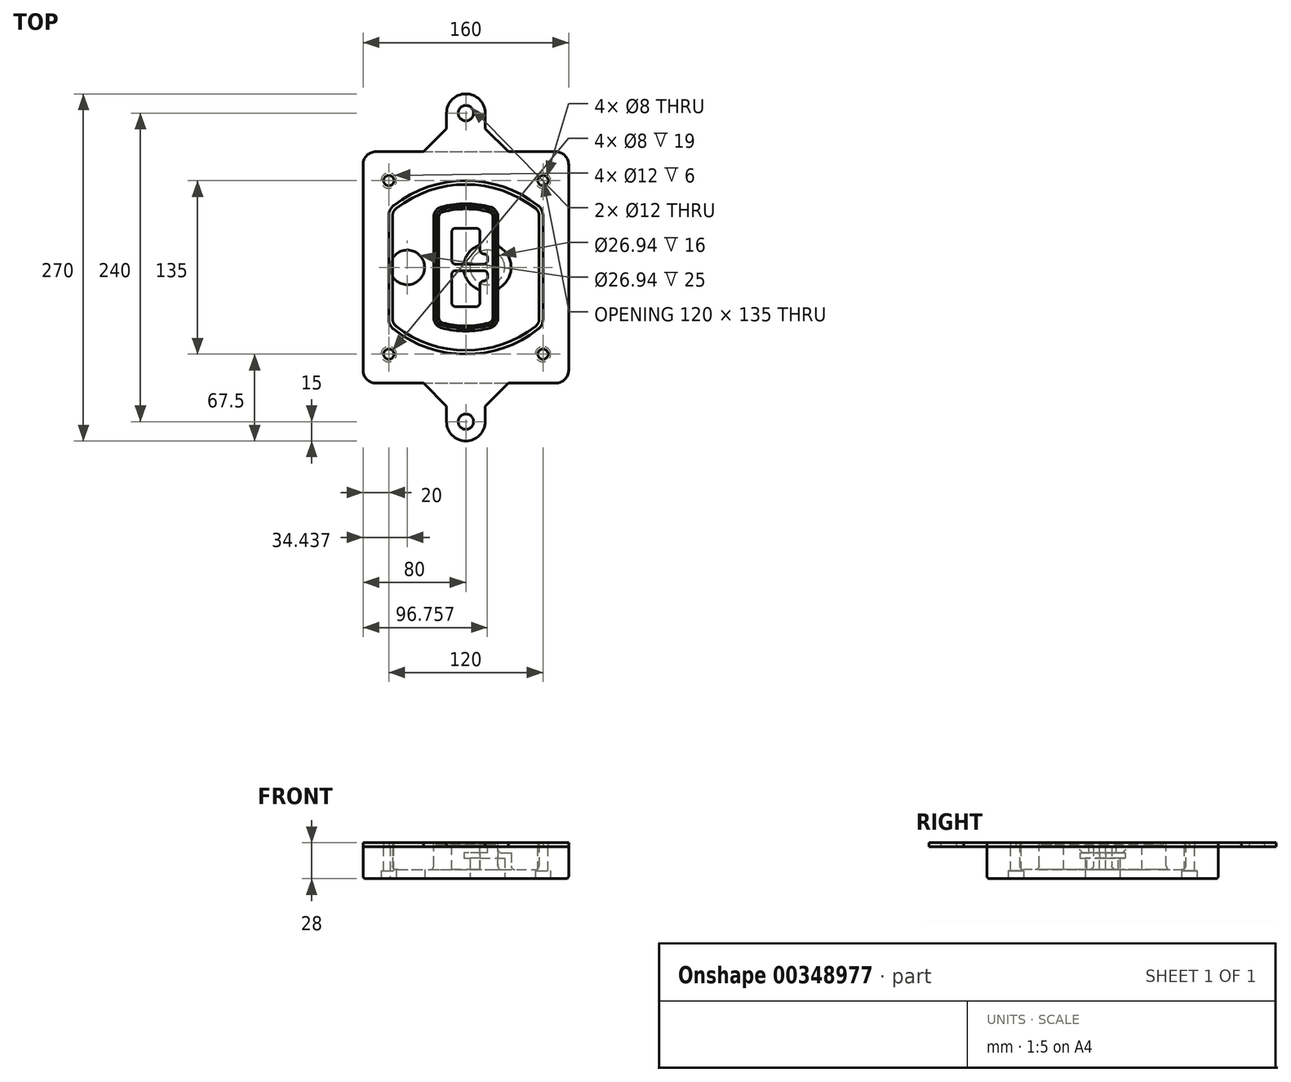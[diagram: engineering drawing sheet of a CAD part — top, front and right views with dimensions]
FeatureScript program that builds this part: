
annotation { "Feature Type Name" : "Feature", "Feature Type Description" : "" }
export const myFeature = defineFeature(function(context is Context, id is Id, definition is map)
    precondition{}
    {
        {
            var Q0;
            Q0=qCreatedBy(makeId("Top.planeOp"),FACE);
            var sketch = newSketch(context, id + "F0", { "sketchPlane" : qUnion([Q0])});
            skPoint(sketch, "E0.rect.middle", {"position": v(0, 0) * mm});
            skLineSegment(sketch, "E1.bottom", {"start": v(-70, -90) * mm, "end": v(70, -90) * mm});
            skLineSegment(sketch, "E1.top", {"start": v(-70, 90) * mm, "end": v(70, 90) * mm});
            skLineSegment(sketch, "E1.left", {"start": v(-80, -80) * mm, "end": v(-80, 80) * mm});
            skLineSegment(sketch, "E1.right", {"start": v(80, -80) * mm, "end": v(80, 80) * mm});
            skLineSegment(sketch, "E2", {"start": v(-80, 90) * mm, "end": v(80, -90) * mm, "construction": true});
            skLineSegment(sketch, "E3", {"start": v(80, 90) * mm, "end": v(-80, -90) * mm, "construction": true});
            skCircle(sketch, "E4", {"center": v(-60, 67.5) * mm, "radius": 4 * mm});
            skCircle(sketch, "E5", {"center": v(60, 67.5) * mm, "radius": 4 * mm});
            skCircle(sketch, "E6", {"center": v(60, -67.5) * mm, "radius": 4 * mm});
            skCircle(sketch, "E7", {"center": v(-60, -67.5) * mm, "radius": 4 * mm});
            skLineSegment(sketch, "E8", {"start": v(-60, 67.5) * mm, "end": v(60, 67.5) * mm, "construction": true});
            skLineSegment(sketch, "E9", {"start": v(60, 67.5) * mm, "end": v(60, -67.5) * mm, "construction": true});
            skLineSegment(sketch, "E10", {"start": v(60, -67.5) * mm, "end": v(-60, -67.5) * mm, "construction": true});
            skLineSegment(sketch, "E11", {"start": v(-60, -67.5) * mm, "end": v(-60, 67.5) * mm, "construction": true});
            skLineSegment(sketch, "E12", {"start": v(-60, 40.3) * mm, "end": v(-60, -40.3) * mm});
            skLineSegment(sketch, "E13", {"start": v(60, 40.3) * mm, "end": v(60, -40.3) * mm});
            skArc(sketch, "E14", {"start": v(56.15, 48.18) * mm, "mid": v(0, 67.5) * mm, "end": v(-56.15, 48.18) * mm});
            skArc(sketch, "E15", {"start": v(-56.15, -48.18) * mm, "mid": v(0, -67.5) * mm, "end": v(56.15, -48.18) * mm});
            skLineSegment(sketch, "E16", {"start": v(-60, 0) * mm, "end": v(60, 0) * mm, "construction": true});
            skPoint(sketch, "E17.visualSharp", {"position": v(-60, -45) * mm});
            skArc(sketch, "E17.filletArc", {"start": v(-60, -40.3) * mm, "mid": v(-58.99, -44.68) * mm, "end": v(-56.15, -48.18) * mm});
            skPoint(sketch, "E18.visualSharp", {"position": v(-60, 45) * mm});
            skArc(sketch, "E18.filletArc", {"start": v(-56.15, 48.18) * mm, "mid": v(-58.99, 44.68) * mm, "end": v(-60, 40.3) * mm});
            skPoint(sketch, "E19.visualSharp", {"position": v(60, 45) * mm});
            skArc(sketch, "E19.filletArc", {"start": v(60, 40.3) * mm, "mid": v(58.99, 44.68) * mm, "end": v(56.15, 48.18) * mm});
            skPoint(sketch, "E20.visualSharp", {"position": v(60, -45) * mm});
            skArc(sketch, "E20.filletArc", {"start": v(56.15, -48.18) * mm, "mid": v(58.99, -44.68) * mm, "end": v(60, -40.3) * mm});
            skPoint(sketch, "E21.visualSharp", {"position": v(-80, 90) * mm});
            skArc(sketch, "E21.filletArc", {"start": v(-70, 90) * mm, "mid": v(-77.07, 87.07) * mm, "end": v(-80, 80) * mm});
            skPoint(sketch, "E22.visualSharp", {"position": v(80, 90) * mm});
            skArc(sketch, "E22.filletArc", {"start": v(80, 80) * mm, "mid": v(77.07, 87.07) * mm, "end": v(70, 90) * mm});
            skPoint(sketch, "E23.visualSharp", {"position": v(80, -90) * mm});
            skArc(sketch, "E23.filletArc", {"start": v(70, -90) * mm, "mid": v(77.07, -87.07) * mm, "end": v(80, -80) * mm});
            skPoint(sketch, "E24.visualSharp", {"position": v(-80, -90) * mm});
            skArc(sketch, "E24.filletArc", {"start": v(-80, -80) * mm, "mid": v(-77.07, -87.07) * mm, "end": v(-70, -90) * mm});
            skArc(sketch, "E25.0", {"start": v(57, 40.3) * mm, "mid": v(56.3, 43.36) * mm, "end": v(54.3, 45.81) * mm});
            skLineSegment(sketch, "E25.1", {"start": v(57, 40.3) * mm, "end": v(57, -40.3) * mm});
            skArc(sketch, "E25.2", {"start": v(54.3, -45.81) * mm, "mid": v(56.3, -43.36) * mm, "end": v(57, -40.3) * mm});
            skArc(sketch, "E25.3", {"start": v(-54.3, -45.81) * mm, "mid": v(0, -64.5) * mm, "end": v(54.3, -45.81) * mm});
            skArc(sketch, "E25.4", {"start": v(-57, -40.3) * mm, "mid": v(-56.3, -43.36) * mm, "end": v(-54.3, -45.81) * mm});
            skArc(sketch, "E25.5", {"start": v(54.3, 45.81) * mm, "mid": v(0, 64.5) * mm, "end": v(-54.3, 45.81) * mm});
            skLineSegment(sketch, "E25.6", {"start": v(-57, 40.3) * mm, "end": v(-57, -40.3) * mm});
            skArc(sketch, "E25.7", {"start": v(-54.3, 45.81) * mm, "mid": v(-56.3, 43.36) * mm, "end": v(-57, 40.3) * mm});
            skArc(sketch, "E26.0", {"start": v(-58.62, 51.33) * mm, "mid": v(-62.58, 46.43) * mm, "end": v(-64, 40.3) * mm});
            skArc(sketch, "E26.1", {"start": v(58.62, 51.33) * mm, "mid": v(0, 71.5) * mm, "end": v(-58.62, 51.33) * mm});
            skArc(sketch, "E26.2", {"start": v(64, 40.3) * mm, "mid": v(62.58, 46.43) * mm, "end": v(58.62, 51.33) * mm});
            skLineSegment(sketch, "E26.3", {"start": v(64, 40.3) * mm, "end": v(64, -40.3) * mm});
            skArc(sketch, "E26.4", {"start": v(58.62, -51.33) * mm, "mid": v(62.58, -46.43) * mm, "end": v(64, -40.3) * mm});
            skLineSegment(sketch, "E26.5", {"start": v(-64, 40.3) * mm, "end": v(-64, -40.3) * mm});
            skArc(sketch, "E26.6", {"start": v(-58.62, -51.33) * mm, "mid": v(0, -71.5) * mm, "end": v(58.62, -51.33) * mm});
            skArc(sketch, "E26.7", {"start": v(-64, -40.3) * mm, "mid": v(-62.58, -46.43) * mm, "end": v(-58.62, -51.33) * mm});
            skSolve(sketch);
        }
        {
            var Q0;
            Q0=makeQuery(id+"F0.imprint","IMPRINT",FACE,{"disambiguationData":[TD([[makeQuery(id+"F0.imprint","IMPRINT",EDGE,{"derivedFrom":sQuery(id+"F0.wireOp",EDGE,"E1.bottom")}),1.0]])]});
            var Q1;
            Q1=makeQuery(id+"F0.imprint","IMPRINT",FACE,{"disambiguationData":[TD([[makeQuery(id+"F0.imprint","IMPRINT",EDGE,{"derivedFrom":sQuery(id+"F0.wireOp",EDGE,"E12")}),1.0]])]});
            var Q2;
            Q2=makeQuery(id+"F0.imprint","IMPRINT",FACE,{"disambiguationData":[TD([[makeQuery(id+"F0.imprint","IMPRINT",EDGE,{"derivedFrom":sQuery(id+"F0.wireOp",EDGE,"E25.0")}),1.0]])]});
            var Q3;
            Q3=makeQuery(id+"F0.imprint","IMPRINT",FACE,{"disambiguationData":[TD([[makeQuery(id+"F0.imprint","IMPRINT",EDGE,{"derivedFrom":sQuery(id+"F0.wireOp",EDGE,"E12")}),-1.0]])]});
            extrude(context, id + "F1", {"entities" : qUnion([Q0, Q1, Q2, Q3]), "oppositeDirection" : true, "depth" : 25 * mm});
        }
        {
            var Q0;
            Q0=makeQuery(id+"F0.imprint","IMPRINT",FACE,{"disambiguationData":[TD([[makeQuery(id+"F0.imprint","IMPRINT",EDGE,{"derivedFrom":sQuery(id+"F0.wireOp",EDGE,"E12")}),1.0]])]});
            extrude(context, id + "F2", {"entities" : qUnion([Q0]), "operationType" : NewBodyOperationType.ADD, "depth" : 3 * mm});
        }
        {
            var Q0;
            Q0=makeQuery(id+"F0.imprint","IMPRINT",FACE,{"disambiguationData":[TD([[makeQuery(id+"F0.imprint","IMPRINT",EDGE,{"derivedFrom":sQuery(id+"F0.wireOp",EDGE,"E25.0")}),1.0]])]});
            extrude(context, id + "F3", {"entities" : qUnion([Q0]), "operationType" : NewBodyOperationType.REMOVE, "oppositeDirection" : true, "depth" : 18 * mm});
        }
        {
            var Q0;
            Q0=makeQuery(id+"F2.opExtrude","CAP_FACE",FACE,{"disambiguationData":[OSD([sQuery(id+"F0.wireOp",EDGE,"E12"),sQuery(id+"F0.wireOp",EDGE,"E13"),sQuery(id+"F0.wireOp",EDGE,"E14"),sQuery(id+"F0.wireOp",EDGE,"E15"),sQuery(id+"F0.wireOp",EDGE,"E17.filletArc"),sQuery(id+"F0.wireOp",EDGE,"E18.filletArc"),sQuery(id+"F0.wireOp",EDGE,"E19.filletArc"),sQuery(id+"F0.wireOp",EDGE,"E20.filletArc"),sQuery(id+"F0.wireOp",EDGE,"E25.0"),sQuery(id+"F0.wireOp",EDGE,"E25.1"),sQuery(id+"F0.wireOp",EDGE,"E25.2"),sQuery(id+"F0.wireOp",EDGE,"E25.3"),sQuery(id+"F0.wireOp",EDGE,"E25.4"),sQuery(id+"F0.wireOp",EDGE,"E25.5"),sQuery(id+"F0.wireOp",EDGE,"E25.6"),sQuery(id+"F0.wireOp",EDGE,"E25.7")])],"isStart":false});
            var sketch = newSketch(context, id + "F4", { "sketchPlane" : qUnion([Q0])});
            skArc(sketch, "E27.0", {"start": v(-19.08, -46.97) * mm, "mid": v(0, -49.5) * mm, "end": v(19.08, -46.97) * mm});
            skArc(sketch, "E28.0", {"start": v(19.08, 46.97) * mm, "mid": v(0, 49.5) * mm, "end": v(-19.08, 46.97) * mm});
            skLineSegment(sketch, "E29", {"start": v(-25, 39.25) * mm, "end": v(-25, -39.25) * mm});
            skLineSegment(sketch, "E30", {"start": v(25, 39.25) * mm, "end": v(25, -39.25) * mm});
            skLineSegment(sketch, "E31", {"start": v(-25, 45.1) * mm, "end": v(25, 45.1) * mm, "construction": true});
            skLineSegment(sketch, "E32", {"start": v(-25, -45.1) * mm, "end": v(25, -45.1) * mm, "construction": true});
            skPoint(sketch, "E33.visualSharp", {"position": v(-25, 45.1) * mm});
            skArc(sketch, "E33.filletArc", {"start": v(-19.08, 46.97) * mm, "mid": v(-23.35, 44.11) * mm, "end": v(-25, 39.25) * mm});
            skPoint(sketch, "E34.visualSharp", {"position": v(25, 45.1) * mm});
            skArc(sketch, "E34.filletArc", {"start": v(25, 39.25) * mm, "mid": v(23.35, 44.11) * mm, "end": v(19.08, 46.97) * mm});
            skPoint(sketch, "E35.visualSharp", {"position": v(25, -45.1) * mm});
            skArc(sketch, "E35.filletArc", {"start": v(19.08, -46.97) * mm, "mid": v(23.35, -44.11) * mm, "end": v(25, -39.25) * mm});
            skPoint(sketch, "E36.visualSharp", {"position": v(-25, -45.1) * mm});
            skArc(sketch, "E36.filletArc", {"start": v(-25, -39.25) * mm, "mid": v(-23.35, -44.11) * mm, "end": v(-19.08, -46.97) * mm});
            skArc(sketch, "E37.0", {"start": v(54.3, 45.81) * mm, "mid": v(0, 64.5) * mm, "end": v(-54.3, 45.81) * mm});
            skArc(sketch, "E37.1", {"start": v(-54.3, 45.81) * mm, "mid": v(-56.3, 43.36) * mm, "end": v(-57, 40.3) * mm});
            skLineSegment(sketch, "E37.2", {"start": v(-57, 40.3) * mm, "end": v(-57, -40.3) * mm});
            skArc(sketch, "E37.3", {"start": v(-57, -40.3) * mm, "mid": v(-56.3, -43.36) * mm, "end": v(-54.3, -45.81) * mm});
            skArc(sketch, "E37.4", {"start": v(-54.3, -45.81) * mm, "mid": v(0, -64.5) * mm, "end": v(54.3, -45.81) * mm});
            skArc(sketch, "E37.5", {"start": v(54.3, -45.81) * mm, "mid": v(56.3, -43.36) * mm, "end": v(57, -40.3) * mm});
            skLineSegment(sketch, "E37.6", {"start": v(57, 40.3) * mm, "end": v(57, -40.3) * mm});
            skArc(sketch, "E37.7", {"start": v(57, 40.3) * mm, "mid": v(56.3, 43.36) * mm, "end": v(54.3, 45.81) * mm});
            skLineSegment(sketch, "E38.0", {"start": v(23, 39.25) * mm, "end": v(23, -39.25) * mm});
            skArc(sketch, "E38.1", {"start": v(18.56, -45.04) * mm, "mid": v(21.76, -42.9) * mm, "end": v(23, -39.25) * mm});
            skArc(sketch, "E38.2", {"start": v(-18.56, -45.04) * mm, "mid": v(0, -47.5) * mm, "end": v(18.56, -45.04) * mm});
            skArc(sketch, "E38.3", {"start": v(-23, -39.25) * mm, "mid": v(-21.76, -42.9) * mm, "end": v(-18.56, -45.04) * mm});
            skLineSegment(sketch, "E38.4", {"start": v(-23, 39.25) * mm, "end": v(-23, -39.25) * mm});
            skArc(sketch, "E38.5", {"start": v(23, 39.25) * mm, "mid": v(21.76, 42.9) * mm, "end": v(18.56, 45.04) * mm});
            skArc(sketch, "E38.6", {"start": v(-18.56, 45.04) * mm, "mid": v(-21.76, 42.9) * mm, "end": v(-23, 39.25) * mm});
            skArc(sketch, "E38.7", {"start": v(18.56, 45.04) * mm, "mid": v(0, 47.5) * mm, "end": v(-18.56, 45.04) * mm});
            skArc(sketch, "E39.0", {"start": v(21, 39.25) * mm, "mid": v(20.18, 41.68) * mm, "end": v(18.04, 43.1) * mm});
            skLineSegment(sketch, "E39.1", {"start": v(21, 39.25) * mm, "end": v(21, -39.25) * mm});
            skArc(sketch, "E39.2", {"start": v(18.04, -43.1) * mm, "mid": v(20.18, -41.68) * mm, "end": v(21, -39.25) * mm});
            skArc(sketch, "E39.3", {"start": v(-18.04, -43.1) * mm, "mid": v(0, -45.5) * mm, "end": v(18.04, -43.1) * mm});
            skArc(sketch, "E39.4", {"start": v(-21, -39.25) * mm, "mid": v(-20.18, -41.68) * mm, "end": v(-18.04, -43.1) * mm});
            skArc(sketch, "E39.5", {"start": v(18.04, 43.1) * mm, "mid": v(0, 45.5) * mm, "end": v(-18.04, 43.1) * mm});
            skLineSegment(sketch, "E39.6", {"start": v(-21, 39.25) * mm, "end": v(-21, -39.25) * mm});
            skArc(sketch, "E39.7", {"start": v(-18.04, 43.1) * mm, "mid": v(-20.18, 41.68) * mm, "end": v(-21, 39.25) * mm});
            skLineSegment(sketch, "E40", {"start": v(-25, 0) * mm, "end": v(25, 0) * mm, "construction": true});
            skLineSegment(sketch, "E41", {"start": v(-11, 5.5) * mm, "end": v(-11, 27.5) * mm});
            skLineSegment(sketch, "E42", {"start": v(-8, 30.5) * mm, "end": v(8, 30.5) * mm});
            skLineSegment(sketch, "E43", {"start": v(11, 27.5) * mm, "end": v(11, 13.5) * mm});
            skLineSegment(sketch, "E44", {"start": v(14, 10.5) * mm, "end": v(14, 10.5) * mm});
            skLineSegment(sketch, "E45", {"start": v(17, 7.5) * mm, "end": v(17, 5.5) * mm});
            skLineSegment(sketch, "E46", {"start": v(14, 2.5) * mm, "end": v(-8, 2.5) * mm});
            skPoint(sketch, "E47.visualSharp", {"position": v(-11, 30.5) * mm});
            skArc(sketch, "E47.filletArc", {"start": v(-8, 30.5) * mm, "mid": v(-10.12, 29.62) * mm, "end": v(-11, 27.5) * mm});
            skPoint(sketch, "E48.visualSharp", {"position": v(11, 30.5) * mm});
            skArc(sketch, "E48.filletArc", {"start": v(11, 27.5) * mm, "mid": v(10.12, 29.62) * mm, "end": v(8, 30.5) * mm});
            skPoint(sketch, "E49.visualSharp", {"position": v(11, 10.5) * mm});
            skArc(sketch, "E49.filletArc", {"start": v(11, 13.5) * mm, "mid": v(11.88, 11.38) * mm, "end": v(14, 10.5) * mm});
            skPoint(sketch, "E50.visualSharp", {"position": v(17, 10.5) * mm});
            skArc(sketch, "E50.filletArc", {"start": v(17, 7.5) * mm, "mid": v(16.12, 9.62) * mm, "end": v(14, 10.5) * mm});
            skPoint(sketch, "E51.visualSharp", {"position": v(17, 2.5) * mm});
            skArc(sketch, "E51.filletArc", {"start": v(14, 2.5) * mm, "mid": v(16.12, 3.38) * mm, "end": v(17, 5.5) * mm});
            skPoint(sketch, "E52.visualSharp", {"position": v(-11, 2.5) * mm});
            skArc(sketch, "E52.filletArc", {"start": v(-11, 5.5) * mm, "mid": v(-10.12, 3.38) * mm, "end": v(-8, 2.5) * mm});
            skLineSegment(sketch, "E53.0.MirrorCS", {"start": v(14, -2.5) * mm, "end": v(-8, -2.5) * mm});
            skArc(sketch, "E54.0.MirrorCS", {"start": v(-11, -5.5) * mm, "mid": v(-10.12, -3.38) * mm, "end": v(-8, -2.5) * mm});
            skLineSegment(sketch, "E55.0.MirrorCS", {"start": v(-11, -5.5) * mm, "end": v(-11, -27.5) * mm});
            skArc(sketch, "E56.0.MirrorCS", {"start": v(-8, -30.5) * mm, "mid": v(-10.12, -29.62) * mm, "end": v(-11, -27.5) * mm});
            skLineSegment(sketch, "E57.0.MirrorCS", {"start": v(-8, -30.5) * mm, "end": v(8, -30.5) * mm});
            skArc(sketch, "E58.0.MirrorCS", {"start": v(11, -27.5) * mm, "mid": v(10.12, -29.62) * mm, "end": v(8, -30.5) * mm});
            skLineSegment(sketch, "E59.0.MirrorCS", {"start": v(11, -27.5) * mm, "end": v(11, -13.5) * mm});
            skArc(sketch, "E60.0.MirrorCS", {"start": v(11, -13.5) * mm, "mid": v(11.88, -11.38) * mm, "end": v(14, -10.5) * mm});
            skArc(sketch, "E61.0.MirrorCS", {"start": v(17, -7.5) * mm, "mid": v(16.12, -9.62) * mm, "end": v(14, -10.5) * mm});
            skLineSegment(sketch, "E62.0.MirrorCS", {"start": v(17, -7.5) * mm, "end": v(17, -5.5) * mm});
            skArc(sketch, "E63.0.MirrorCS", {"start": v(14, -2.5) * mm, "mid": v(16.12, -3.38) * mm, "end": v(17, -5.5) * mm});
            skSolve(sketch);
        }
        {
            var Q0;
            Q0=makeQuery(id+"F4.imprint","IMPRINT",FACE,{"disambiguationData":[TD([[makeQuery(id+"F4.imprint","IMPRINT",EDGE,{"derivedFrom":sQuery(id+"F4.wireOp",EDGE,"E27.0")}),1.0]])]});
            var Q1;
            Q1=makeQuery(id+"F4.imprint","IMPRINT",FACE,{"disambiguationData":[TD([[makeQuery(id+"F4.imprint","IMPRINT",EDGE,{"derivedFrom":sQuery(id+"F4.wireOp",EDGE,"E38.0")}),-1.0]])]});
            var Q2;
            Q2=makeQuery(id+"F4.imprint","IMPRINT",FACE,{"disambiguationData":[TD([[makeQuery(id+"F4.imprint","IMPRINT",EDGE,{"derivedFrom":sQuery(id+"F4.wireOp",EDGE,"E39.0")}),1.0]])]});
            extrude(context, id + "F5", {"entities" : qUnion([Q0, Q1, Q2]), "operationType" : NewBodyOperationType.ADD, "endBound" : BoundingType.UP_TO_NEXT, "oppositeDirection" : true, "depth" : 25 * mm});
        }
        {
            var Q0;
            Q0=makeQuery(id+"F4.imprint","IMPRINT",FACE,{"disambiguationData":[TD([[makeQuery(id+"F4.imprint","IMPRINT",EDGE,{"derivedFrom":sQuery(id+"F4.wireOp",EDGE,"E38.0")}),-1.0]])]});
            extrude(context, id + "F6", {"entities" : qUnion([Q0]), "operationType" : NewBodyOperationType.REMOVE, "oppositeDirection" : true, "depth" : 2 * mm});
        }
        {
            var Q0;
            Q0=makeQuery(id+"F1.opExtrude","CAP_FACE",FACE,{"disambiguationData":[OSD([sQuery(id+"F0.wireOp",EDGE,"E1.bottom"),sQuery(id+"F0.wireOp",EDGE,"E1.top"),sQuery(id+"F0.wireOp",EDGE,"E1.left"),sQuery(id+"F0.wireOp",EDGE,"E1.right"),sQuery(id+"F0.wireOp",EDGE,"E4"),sQuery(id+"F0.wireOp",EDGE,"E5"),sQuery(id+"F0.wireOp",EDGE,"E6"),sQuery(id+"F0.wireOp",EDGE,"E7"),sQuery(id+"F0.wireOp",EDGE,"E21.filletArc"),sQuery(id+"F0.wireOp",EDGE,"E22.filletArc"),sQuery(id+"F0.wireOp",EDGE,"E23.filletArc"),sQuery(id+"F0.wireOp",EDGE,"E24.filletArc")])],"isStart":false});
            var sketch = newSketch(context, id + "F7", { "sketchPlane" : qUnion([Q0])});
            skCircle(sketch, "E64", {"center": v(16.76, 0) * mm, "radius": 13.47 * mm});
            skCircle(sketch, "E65", {"center": v(-45.56, 0) * mm, "radius": 13.47 * mm});
            skLineSegment(sketch, "E66", {"start": v(80, 0) * mm, "end": v(-80, 0) * mm});
            skCircle(sketch, "E67", {"center": v(16.76, 0) * mm, "radius": 18.47 * mm});
            skCircle(sketch, "E68", {"center": v(60, -67.5) * mm, "radius": 6 * mm});
            skCircle(sketch, "E69", {"center": v(-60, -67.5) * mm, "radius": 6 * mm});
            skCircle(sketch, "E70", {"center": v(-60, 67.5) * mm, "radius": 6 * mm});
            skCircle(sketch, "E71", {"center": v(60, 67.5) * mm, "radius": 6 * mm});
            skSolve(sketch);
        }
        {
            var Q0;
            {var subQ1=sQuery(id+"F7.wireOp",EDGE,"E66");var subQ4=sQuery(id+"F7.wireOp",EDGE,"E64");var subQ6=makeQuery(id+"F7.imprint","INTERSECT",VERTEX,{"disambiguationData":[OD(0.0)],"derivedFrom":[subQ4,subQ1]});Q0=makeQuery(id+"F7.imprint","IMPRINT",FACE,{"disambiguationData":[TD([[makeQuery(id+"F7.imprint","IMPRINT",EDGE,{"disambiguationData":[TD([[subQ6,-1.0]])],"derivedFrom":subQ4}),-1.0]])]});}
            var Q1;
            {var subQ0=sQuery(id+"F7.wireOp",EDGE,"E66");var subQ1=sQuery(id+"F7.wireOp",EDGE,"E64");var subQ3=makeQuery(id+"F7.imprint","INTERSECT",VERTEX,{"disambiguationData":[OD(0.0)],"derivedFrom":[subQ1,subQ0]});Q1=makeQuery(id+"F7.imprint","IMPRINT",FACE,{"disambiguationData":[TD([[makeQuery(id+"F7.imprint","IMPRINT",EDGE,{"disambiguationData":[TD([[subQ3,-1.0]])],"derivedFrom":subQ1}),1.0]])]});}
            var Q2;
            {var subQ0=sQuery(id+"F7.wireOp",EDGE,"E66");var subQ1=sQuery(id+"F7.wireOp",EDGE,"E64");var subQ3=makeQuery(id+"F7.imprint","INTERSECT",VERTEX,{"disambiguationData":[OD(0.0)],"derivedFrom":[subQ1,subQ0]});Q2=makeQuery(id+"F7.imprint","IMPRINT",FACE,{"disambiguationData":[TD([[makeQuery(id+"F7.imprint","IMPRINT",EDGE,{"disambiguationData":[TD([[subQ3,1.0]])],"derivedFrom":subQ1}),1.0]])]});}
            var Q3;
            {var subQ1=sQuery(id+"F7.wireOp",EDGE,"E66");var subQ4=sQuery(id+"F7.wireOp",EDGE,"E64");var subQ6=makeQuery(id+"F7.imprint","INTERSECT",VERTEX,{"disambiguationData":[OD(0.0)],"derivedFrom":[subQ4,subQ1]});Q3=makeQuery(id+"F7.imprint","IMPRINT",FACE,{"disambiguationData":[TD([[makeQuery(id+"F7.imprint","IMPRINT",EDGE,{"disambiguationData":[TD([[subQ6,1.0]])],"derivedFrom":subQ4}),-1.0]])]});}
            extrude(context, id + "F8", {"entities" : qUnion([Q0, Q1, Q2, Q3]), "operationType" : NewBodyOperationType.ADD, "oppositeDirection" : true, "depth" : 20 * mm});
        }
        {
            var Q0;
            {var subQ0=sQuery(id+"F7.wireOp",EDGE,"E66");var subQ1=sQuery(id+"F7.wireOp",EDGE,"E64");var subQ3=makeQuery(id+"F7.imprint","INTERSECT",VERTEX,{"disambiguationData":[OD(0.0)],"derivedFrom":[subQ1,subQ0]});Q0=makeQuery(id+"F7.imprint","IMPRINT",FACE,{"disambiguationData":[TD([[makeQuery(id+"F7.imprint","IMPRINT",EDGE,{"disambiguationData":[TD([[subQ3,-1.0]])],"derivedFrom":subQ1}),1.0]])]});}
            var Q1;
            {var subQ0=sQuery(id+"F7.wireOp",EDGE,"E66");var subQ1=sQuery(id+"F7.wireOp",EDGE,"E64");var subQ3=makeQuery(id+"F7.imprint","INTERSECT",VERTEX,{"disambiguationData":[OD(0.0)],"derivedFrom":[subQ1,subQ0]});Q1=makeQuery(id+"F7.imprint","IMPRINT",FACE,{"disambiguationData":[TD([[makeQuery(id+"F7.imprint","IMPRINT",EDGE,{"disambiguationData":[TD([[subQ3,1.0]])],"derivedFrom":subQ1}),1.0]])]});}
            extrude(context, id + "F9", {"entities" : qUnion([Q0, Q1]), "operationType" : NewBodyOperationType.REMOVE, "oppositeDirection" : true, "depth" : 16 * mm});
        }
        {
            var Q0;
            {var subQ0=sQuery(id+"F7.wireOp",EDGE,"E66");var subQ1=sQuery(id+"F7.wireOp",EDGE,"E65");var subQ3=makeQuery(id+"F7.imprint","INTERSECT",VERTEX,{"disambiguationData":[OD(0.0)],"derivedFrom":[subQ1,subQ0]});Q0=makeQuery(id+"F7.imprint","IMPRINT",FACE,{"disambiguationData":[TD([[makeQuery(id+"F7.imprint","IMPRINT",EDGE,{"disambiguationData":[TD([[subQ3,-1.0]])],"derivedFrom":subQ1}),1.0]])]});}
            var Q1;
            {var subQ0=sQuery(id+"F7.wireOp",EDGE,"E66");var subQ1=sQuery(id+"F7.wireOp",EDGE,"E65");var subQ3=makeQuery(id+"F7.imprint","INTERSECT",VERTEX,{"disambiguationData":[OD(0.0)],"derivedFrom":[subQ1,subQ0]});Q1=makeQuery(id+"F7.imprint","IMPRINT",FACE,{"disambiguationData":[TD([[makeQuery(id+"F7.imprint","IMPRINT",EDGE,{"disambiguationData":[TD([[subQ3,1.0]])],"derivedFrom":subQ1}),1.0]])]});}
            extrude(context, id + "F10", {"entities" : qUnion([Q0, Q1]), "operationType" : NewBodyOperationType.REMOVE, "oppositeDirection" : true, "depth" : 25 * mm});
        }
        {
            var Q0;
            Q0=makeQuery(id+"F7.imprint","IMPRINT",FACE,{"disambiguationData":[TD([[makeQuery(id+"F7.imprint","IMPRINT",EDGE,{"derivedFrom":sQuery(id+"F7.wireOp",EDGE,"E68")}),1.0]])]});
            var Q1;
            Q1=makeQuery(id+"F7.imprint","IMPRINT",FACE,{"disambiguationData":[TD([[makeQuery(id+"F7.imprint","IMPRINT",EDGE,{"derivedFrom":makeQuery(id+"F1.opExtrude","CAP_EDGE",EDGE,{"disambiguationData":[OSD([sQuery(id+"F0.wireOp",EDGE,"E5")])],"isStart":false})}),-1.0]])]});
            var Q2;
            Q2=makeQuery(id+"F7.imprint","IMPRINT",FACE,{"disambiguationData":[TD([[makeQuery(id+"F7.imprint","IMPRINT",EDGE,{"derivedFrom":sQuery(id+"F7.wireOp",EDGE,"E69")}),1.0]])]});
            var Q3;
            Q3=makeQuery(id+"F7.imprint","IMPRINT",FACE,{"disambiguationData":[TD([[makeQuery(id+"F7.imprint","IMPRINT",EDGE,{"derivedFrom":makeQuery(id+"F1.opExtrude","CAP_EDGE",EDGE,{"disambiguationData":[OSD([sQuery(id+"F0.wireOp",EDGE,"E4")])],"isStart":false})}),-1.0]])]});
            var Q4;
            Q4=makeQuery(id+"F7.imprint","IMPRINT",FACE,{"disambiguationData":[TD([[makeQuery(id+"F7.imprint","IMPRINT",EDGE,{"derivedFrom":sQuery(id+"F7.wireOp",EDGE,"E70")}),1.0]])]});
            var Q5;
            Q5=makeQuery(id+"F7.imprint","IMPRINT",FACE,{"disambiguationData":[TD([[makeQuery(id+"F7.imprint","IMPRINT",EDGE,{"derivedFrom":makeQuery(id+"F1.opExtrude","CAP_EDGE",EDGE,{"disambiguationData":[OSD([sQuery(id+"F0.wireOp",EDGE,"E7")])],"isStart":false})}),-1.0]])]});
            var Q6;
            Q6=makeQuery(id+"F7.imprint","IMPRINT",FACE,{"disambiguationData":[TD([[makeQuery(id+"F7.imprint","IMPRINT",EDGE,{"derivedFrom":sQuery(id+"F7.wireOp",EDGE,"E71")}),1.0]])]});
            var Q7;
            Q7=makeQuery(id+"F7.imprint","IMPRINT",FACE,{"disambiguationData":[TD([[makeQuery(id+"F7.imprint","IMPRINT",EDGE,{"derivedFrom":makeQuery(id+"F1.opExtrude","CAP_EDGE",EDGE,{"disambiguationData":[OSD([sQuery(id+"F0.wireOp",EDGE,"E6")])],"isStart":false})}),-1.0]])]});
            extrude(context, id + "F11", {"entities" : qUnion([Q0, Q1, Q2, Q3, Q4, Q5, Q6, Q7]), "operationType" : NewBodyOperationType.REMOVE, "oppositeDirection" : true, "depth" : 6 * mm});
        }
        {
            var Q0;
            Q0=makeQuery(id+"F9.boolean.opBoolean","COPY",FACE,{"derivedFrom":makeQuery(id+"F9.opExtrude","CAP_FACE",FACE,{"disambiguationData":[OSD([sQuery(id+"F7.wireOp",EDGE,"E64")])],"isStart":false})});
            var sketch = newSketch(context, id + "F12", { "sketchPlane" : qUnion([Q0])});
            skArc(sketch, "E72.0", {"start": v(11, 17.55) * mm, "mid": v(2.57, 11.82) * mm, "end": v(-1.54, 2.5) * mm});
            skArc(sketch, "E72.1", {"start": v(-1.54, -2.5) * mm, "mid": v(2.57, -11.82) * mm, "end": v(11, -17.55) * mm});
            skLineSegment(sketch, "E73", {"start": v(-1.54, -2.5) * mm, "end": v(14, -2.5) * mm});
            skLineSegment(sketch, "E74.0", {"start": v(14, 2.5) * mm, "end": v(-1.54, 2.5) * mm});
            skArc(sketch, "E74.1", {"start": v(14, 2.5) * mm, "mid": v(16.12, 3.38) * mm, "end": v(17, 5.5) * mm});
            skLineSegment(sketch, "E74.2", {"start": v(17, 7.5) * mm, "end": v(17, 5.5) * mm});
            skArc(sketch, "E74.3", {"start": v(17, 7.5) * mm, "mid": v(16.12, 9.62) * mm, "end": v(14, 10.5) * mm});
            skArc(sketch, "E74.4", {"start": v(11, 13.5) * mm, "mid": v(11.88, 11.38) * mm, "end": v(14, 10.5) * mm});
            skLineSegment(sketch, "E74.5", {"start": v(11, 17.55) * mm, "end": v(11, 13.5) * mm});
            skLineSegment(sketch, "E74.7", {"start": v(14, -2.5) * mm, "end": v(-1.54, -2.5) * mm});
            skArc(sketch, "E74.8", {"start": v(14, -2.5) * mm, "mid": v(16.12, -3.38) * mm, "end": v(17, -5.5) * mm});
            skLineSegment(sketch, "E74.9", {"start": v(17, -7.5) * mm, "end": v(17, -5.5) * mm});
            skArc(sketch, "E74.10", {"start": v(17, -7.5) * mm, "mid": v(16.12, -9.62) * mm, "end": v(14, -10.5) * mm});
            skArc(sketch, "E74.11", {"start": v(11, -13.5) * mm, "mid": v(11.88, -11.38) * mm, "end": v(14, -10.5) * mm});
            skLineSegment(sketch, "E74.12", {"start": v(11, -17.55) * mm, "end": v(11, -13.5) * mm});
            skPoint(sketch, "E75.orphan", {"position": v(11, -27.5) * mm});
            skPoint(sketch, "E76.orphan", {"position": v(-8, -2.5) * mm});
            skPoint(sketch, "E77.orphan", {"position": v(-8, 2.5) * mm});
            skPoint(sketch, "E78.orphan", {"position": v(11, 27.5) * mm});
            skSolve(sketch);
        }
        {
            var Q0;
            {var subQ7=sQuery(id+"F12.wireOp",EDGE,"E72.0");var subQ14=sQuery(id+"F12.wireOp",EDGE,"E72.1");var subQ16=sQuery(id+"F12.wireOp",EDGE,"E74.1");var subQ18=sQuery(id+"F12.wireOp",EDGE,"E74.8");Q0=qUnion([makeQuery(id+"F12.imprint","IMPRINT",FACE,{"disambiguationData":[TD([[makeQuery(id+"F12.imprint","IMPRINT",EDGE,{"derivedFrom":subQ7}),1.0]])]}),makeQuery(id+"F12.imprint","IMPRINT",FACE,{"disambiguationData":[TD([[makeQuery(id+"F12.imprint","IMPRINT",EDGE,{"derivedFrom":subQ14}),1.0]])]}),makeQuery(id+"F12.imprint","IMPRINT",FACE,{"disambiguationData":[TD([[makeQuery(id+"F12.imprint","IMPRINT",EDGE,{"derivedFrom":subQ16}),1.0]])]}),makeQuery(id+"F12.imprint","IMPRINT",FACE,{"disambiguationData":[TD([[makeQuery(id+"F12.imprint","IMPRINT",EDGE,{"derivedFrom":subQ18}),-1.0]])]})]);}
            var Q1;
            Q1=makeQuery(id+"F5.boolean.opBoolean","SPLIT",FACE,{"disambiguationData":[TD([makeQuery(id+"F5.opExtrude","SWEPT_FACE",FACE,{"disambiguationData":[OSD([sQuery(id+"F4.wireOp",EDGE,"E41")])]})])],"derivedFrom":makeQuery(id+"F3.boolean.opBoolean","COPY",FACE,{"derivedFrom":makeQuery(id+"F3.opExtrude","CAP_FACE",FACE,{"disambiguationData":[OSD([sQuery(id+"F0.wireOp",EDGE,"E25.0"),sQuery(id+"F0.wireOp",EDGE,"E25.1"),sQuery(id+"F0.wireOp",EDGE,"E25.2"),sQuery(id+"F0.wireOp",EDGE,"E25.3"),sQuery(id+"F0.wireOp",EDGE,"E25.4"),sQuery(id+"F0.wireOp",EDGE,"E25.5"),sQuery(id+"F0.wireOp",EDGE,"E25.6"),sQuery(id+"F0.wireOp",EDGE,"E25.7")])],"isStart":false})})});
            extrude(context, id + "F13", {"entities" : qUnion([Q0]), "operationType" : NewBodyOperationType.REMOVE, "endBound" : BoundingType.UP_TO_SURFACE, "endBoundEntityFace" : qUnion([Q1]), "depth" : 25 * mm});
        }
        {
            var Q0;
            Q0=makeQuery(id+"F3.boolean.opBoolean","COPY",EDGE,{"derivedFrom":makeQuery(id+"F3.opExtrude","CAP_EDGE",EDGE,{"disambiguationData":[OSD([sQuery(id+"F0.wireOp",EDGE,"E25.6")])],"isStart":false})});
            var Q1;
            Q1=makeQuery(id+"F8.boolean.opBoolean","INTERSECT",EDGE,{"derivedFrom":[makeQuery(id+"F5.opExtrude","SWEPT_FACE",FACE,{"disambiguationData":[OSD([sQuery(id+"F4.wireOp",EDGE,"E30")])]}),makeQuery(id+"F8.opExtrude","CAP_FACE",FACE,{"disambiguationData":[OSD([sQuery(id+"F7.wireOp",EDGE,"E67")])],"isStart":false})]});
            var Q2;
            Q2=makeQuery(id+"F8.boolean.opBoolean","INTERSECT",EDGE,{"disambiguationData":[OD(1.0)],"derivedFrom":[makeQuery(id+"F5.opExtrude","SWEPT_FACE",FACE,{"disambiguationData":[OSD([sQuery(id+"F4.wireOp",EDGE,"E30")])]}),makeQuery(id+"F8.opExtrude","SWEPT_FACE",FACE,{"disambiguationData":[OSD([sQuery(id+"F7.wireOp",EDGE,"E67")])]})]});
            var Q3;
            {var subQ0=sQuery(id+"F4.wireOp",EDGE,"E30");Q3=makeQuery(id+"F8.boolean.opBoolean","SPLIT",EDGE,{"disambiguationData":[TD([makeQuery(id+"F5.opExtrude","SWEPT_FACE",FACE,{"disambiguationData":[OSD([sQuery(id+"F4.wireOp",EDGE,"E35.filletArc")])]})])],"derivedFrom":makeQuery(id+"F5.opExtrude","CAP_EDGE",EDGE,{"disambiguationData":[OSD([subQ0])],"isStart":false})});}
            var Q4;
            {var subQ0=sQuery(id+"F0.wireOp",EDGE,"E25.7");var subQ1=sQuery(id+"F0.wireOp",EDGE,"E25.1");var subQ2=sQuery(id+"F0.wireOp",EDGE,"E25.6");var subQ3=sQuery(id+"F0.wireOp",EDGE,"E25.5");var subQ4=sQuery(id+"F0.wireOp",EDGE,"E25.4");var subQ5=sQuery(id+"F0.wireOp",EDGE,"E25.0");var subQ6=sQuery(id+"F0.wireOp",EDGE,"E25.2");var subQ7=sQuery(id+"F0.wireOp",EDGE,"E25.3");Q4=makeQuery(id+"F8.boolean.opBoolean","INTERSECT",EDGE,{"derivedFrom":[makeQuery(id+"F5.boolean.opBoolean","SPLIT",FACE,{"disambiguationData":[TD([makeQuery(id+"F2.opExtrude","SWEPT_FACE",FACE,{"disambiguationData":[OSD([subQ5])]})])],"derivedFrom":makeQuery(id+"F3.boolean.opBoolean","COPY",FACE,{"derivedFrom":makeQuery(id+"F3.opExtrude","CAP_FACE",FACE,{"disambiguationData":[OSD([subQ5,subQ1,subQ6,subQ7,subQ4,subQ3,subQ2,subQ0])],"isStart":false})})}),makeQuery(id+"F8.opExtrude","SWEPT_FACE",FACE,{"disambiguationData":[OSD([sQuery(id+"F7.wireOp",EDGE,"E67")])]})]});}
            var Q5;
            Q5=makeQuery(id+"F8.boolean.opBoolean","INTERSECT",EDGE,{"disambiguationData":[OD(0.0)],"derivedFrom":[makeQuery(id+"F5.opExtrude","SWEPT_FACE",FACE,{"disambiguationData":[OSD([sQuery(id+"F4.wireOp",EDGE,"E30")])]}),makeQuery(id+"F8.opExtrude","SWEPT_FACE",FACE,{"disambiguationData":[OSD([sQuery(id+"F7.wireOp",EDGE,"E67")])]})]});
            fillet(context, id + "F14", {"entities" : qUnion([Q0, Q1, Q2, Q3, Q4, Q5]), "radius" : 3 * mm, "tangentPropagation" : true, "allowEdgeOverflow" : false});
        }
        {
            var Q0;
            Q0=makeQuery(id+"F1.opExtrude","CAP_EDGE",EDGE,{"disambiguationData":[OSD([sQuery(id+"F0.wireOp",EDGE,"E1.bottom")])],"isStart":false});
            fillet(context, id + "F15", {"entities" : qUnion([Q0]), "radius" : 2 * mm, "tangentPropagation" : true, "allowEdgeOverflow" : false});
        }
        {
            var Q0;
            {var subQ0=sQuery(id+"F0.wireOp",EDGE,"E21.filletArc");var subQ1=sQuery(id+"F0.wireOp",EDGE,"E7");var subQ2=sQuery(id+"F0.wireOp",EDGE,"E6");var subQ3=sQuery(id+"F0.wireOp",EDGE,"E5");var subQ4=sQuery(id+"F0.wireOp",EDGE,"E4");var subQ5=sQuery(id+"F0.wireOp",EDGE,"E22.filletArc");var subQ6=sQuery(id+"F0.wireOp",EDGE,"E1.bottom");var subQ7=sQuery(id+"F0.wireOp",EDGE,"E1.right");var subQ8=sQuery(id+"F0.wireOp",EDGE,"E1.top");var subQ9=sQuery(id+"F0.wireOp",EDGE,"E1.left");var subQ10=sQuery(id+"F0.wireOp",EDGE,"E23.filletArc");var subQ11=sQuery(id+"F0.wireOp",EDGE,"E24.filletArc");Q0=makeQuery(id+"F2.boolean.opBoolean","SPLIT",FACE,{"disambiguationData":[TD([makeQuery(id+"F1.opExtrude","SWEPT_FACE",FACE,{"disambiguationData":[OSD([subQ6])]})])],"derivedFrom":makeQuery(id+"F1.opExtrude","CAP_FACE",FACE,{"disambiguationData":[OSD([subQ6,subQ8,subQ9,subQ7,subQ4,subQ3,subQ2,subQ1,subQ0,subQ5,subQ10,subQ11])],"isStart":true})});}
            var sketch = newSketch(context, id + "F16", { "sketchPlane" : qUnion([Q0])});
            skLineSegment(sketch, "E79", {"start": v(0, 90) * mm, "end": v(0, 120) * mm, "construction": true});
            skCircle(sketch, "E80", {"center": v(0, 120) * mm, "radius": 6 * mm});
            skArc(sketch, "E81", {"start": v(15, 120) * mm, "mid": v(0, 135) * mm, "end": v(-15, 120) * mm});
            skLineSegment(sketch, "E82", {"start": v(-15, 120) * mm, "end": v(-15, 108) * mm});
            skLineSegment(sketch, "E83", {"start": v(15, 120) * mm, "end": v(15, 108) * mm});
            skLineSegment(sketch, "E84", {"start": v(-15, 108) * mm, "end": v(-33, 90) * mm});
            skLineSegment(sketch, "E85", {"start": v(15, 108) * mm, "end": v(33, 90) * mm});
            skLineSegment(sketch, "E86", {"start": v(80, 0) * mm, "end": v(-80, 0) * mm, "construction": true});
            skLineSegment(sketch, "E87.MirrorCS", {"start": v(15, -108) * mm, "end": v(33, -90) * mm});
            skLineSegment(sketch, "E88.MirrorCS", {"start": v(-15, -108) * mm, "end": v(-33, -90) * mm});
            skLineSegment(sketch, "E89.MirrorCS", {"start": v(15, -120) * mm, "end": v(15, -108) * mm});
            skLineSegment(sketch, "E90.MirrorCS", {"start": v(-15, -120) * mm, "end": v(-15, -108) * mm});
            skArc(sketch, "E91.MirrorCS", {"start": v(15, -120) * mm, "mid": v(0, -135) * mm, "end": v(-15, -120) * mm});
            skCircle(sketch, "E92.MirrorC", {"center": v(0, -120) * mm, "radius": 6 * mm});
            skLineSegment(sketch, "E93.MirrorCS", {"start": v(0, -90) * mm, "end": v(0, -120) * mm, "construction": true});
            skSolve(sketch);
        }
        {
            var Q0;
            Q0=makeQuery(id+"F16.imprint","IMPRINT",FACE,{"disambiguationData":[TD([[makeQuery(id+"F16.imprint","IMPRINT",EDGE,{"derivedFrom":sQuery(id+"F16.wireOp",EDGE,"E80")}),-1.0]])]});
            var Q1;
            {var subQ1=sQuery(id+"F16.wireOp",EDGE,"E87.MirrorCS");Q1=makeQuery(id+"F16.imprint","IMPRINT",FACE,{"disambiguationData":[TD([[makeQuery(id+"F16.imprint","IMPRINT",EDGE,{"derivedFrom":subQ1}),1.0]])]});}
            var Q2;
            Q2=makeQuery(id+"F16.imprint","IMPRINT",FACE,{"disambiguationData":[TD([[makeQuery(id+"F16.imprint","IMPRINT",EDGE,{"derivedFrom":makeQuery(id+"F1.opExtrude","CAP_EDGE",EDGE,{"disambiguationData":[OSD([sQuery(id+"F0.wireOp",EDGE,"E1.left")])],"isStart":true})}),-1.0]])]});
            var Q3;
            Q3=makeQuery(id+"F2.opExtrude","CAP_FACE",FACE,{"disambiguationData":[OSD([sQuery(id+"F0.wireOp",EDGE,"E12"),sQuery(id+"F0.wireOp",EDGE,"E13"),sQuery(id+"F0.wireOp",EDGE,"E14"),sQuery(id+"F0.wireOp",EDGE,"E15"),sQuery(id+"F0.wireOp",EDGE,"E17.filletArc"),sQuery(id+"F0.wireOp",EDGE,"E18.filletArc"),sQuery(id+"F0.wireOp",EDGE,"E19.filletArc"),sQuery(id+"F0.wireOp",EDGE,"E20.filletArc"),sQuery(id+"F0.wireOp",EDGE,"E25.0"),sQuery(id+"F0.wireOp",EDGE,"E25.1"),sQuery(id+"F0.wireOp",EDGE,"E25.2"),sQuery(id+"F0.wireOp",EDGE,"E25.3"),sQuery(id+"F0.wireOp",EDGE,"E25.4"),sQuery(id+"F0.wireOp",EDGE,"E25.5"),sQuery(id+"F0.wireOp",EDGE,"E25.6"),sQuery(id+"F0.wireOp",EDGE,"E25.7")])],"isStart":false});
            extrude(context, id + "F17", {"entities" : qUnion([Q0, Q1, Q2]), "endBound" : BoundingType.UP_TO_SURFACE, "endBoundEntityFace" : qUnion([Q3]), "depth" : 25 * mm});
        }
    });
